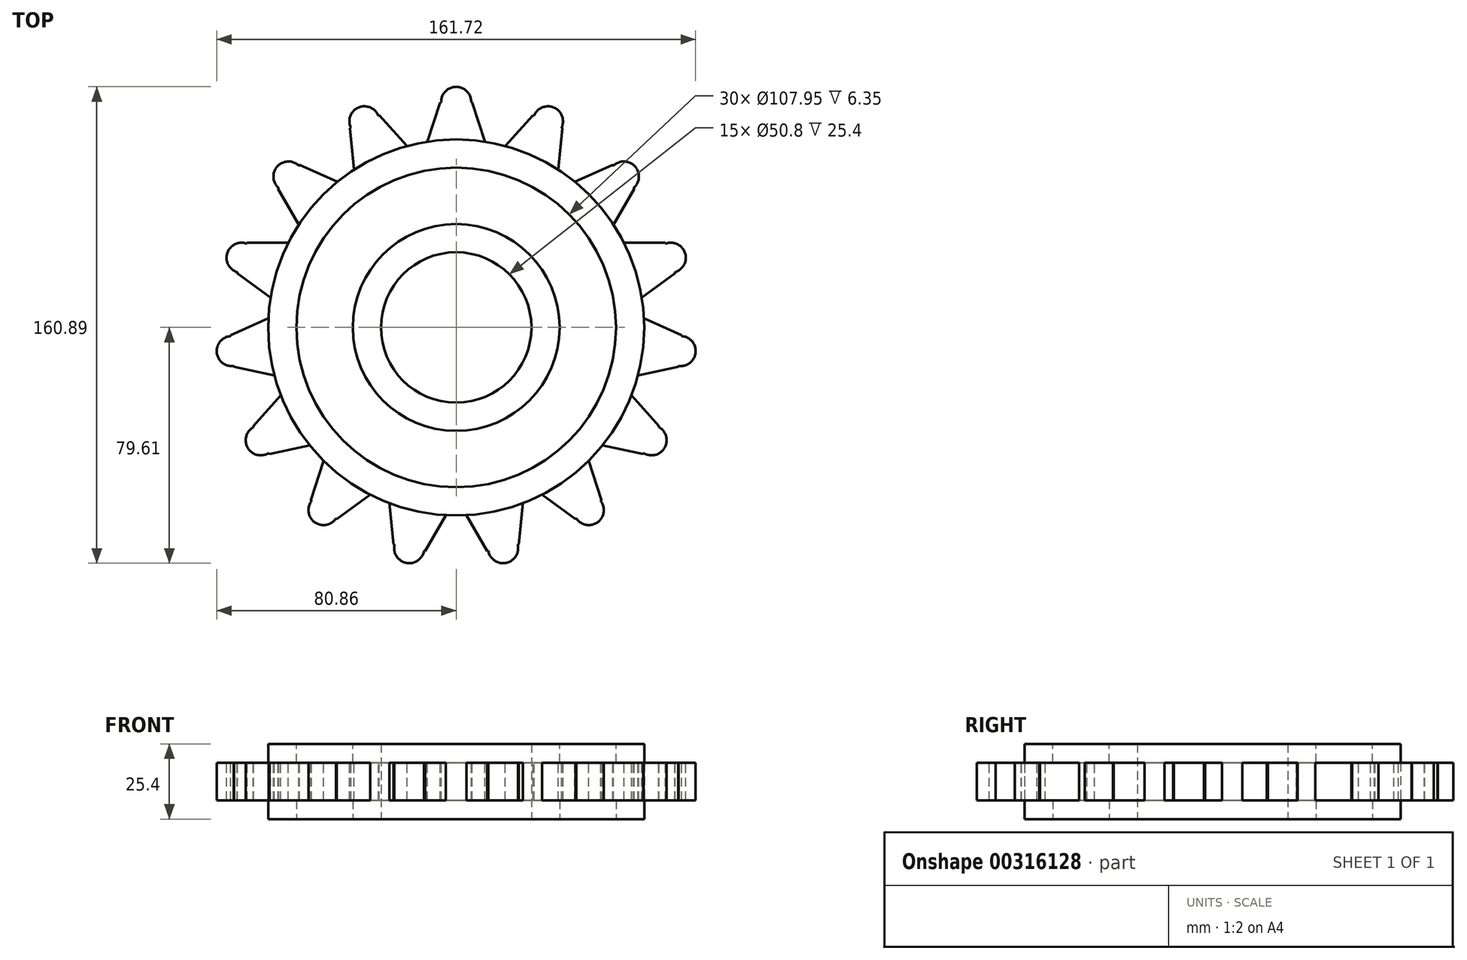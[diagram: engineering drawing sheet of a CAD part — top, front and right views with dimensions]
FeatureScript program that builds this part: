
annotation { "Feature Type Name" : "Feature", "Feature Type Description" : "" }
export const myFeature = defineFeature(function(context is Context, id is Id, definition is map)
    precondition{}
    {
        {
            var Q0;
            Q0=qCreatedBy(makeId("Top.planeOp"),FACE);
            var sketch = newSketch(context, id + "F0", { "sketchPlane" : qUnion([Q0])});
            skCircle(sketch, "E0", {"center": v(0, 0) * mm, "radius": 25.4 * mm});
            skCircle(sketch, "E1", {"center": v(0, 0) * mm, "radius": 63.5 * mm});
            skSolve(sketch);
        }
        {
            var Q0;
            Q0=makeQuery(id+"F0.imprint","IMPRINT",FACE,{"disambiguationData":[TD([[makeQuery(id+"F0.imprint","IMPRINT",EDGE,{"derivedFrom":sQuery(id+"F0.wireOp",EDGE,"E0")}),-1.0]])]});
            extrude(context, id + "F1", {"entities" : qUnion([Q0]), "depth" : 25.4 * mm});
        }
        {
            var Q0;
            Q0=makeQuery(id+"F1.opExtrude","CAP_FACE",FACE,{"disambiguationData":[OSD([sQuery(id+"F0.wireOp",EDGE,"E0"),sQuery(id+"F0.wireOp",EDGE,"E1")])],"isStart":false});
            var sketch = newSketch(context, id + "F2", { "sketchPlane" : qUnion([Q0])});
            skCircle(sketch, "E2", {"center": v(0, 0) * mm, "radius": 53.98 * mm});
            skCircle(sketch, "E3", {"center": v(0, 0) * mm, "radius": 34.93 * mm});
            skSolve(sketch);
        }
        {
            var Q0;
            Q0=makeQuery(id+"F2.imprint","IMPRINT",FACE,{"disambiguationData":[TD([[makeQuery(id+"F2.imprint","IMPRINT",EDGE,{"derivedFrom":sQuery(id+"F2.wireOp",EDGE,"E2")}),1.0]])]});
            extrude(context, id + "F3", {"entities" : qUnion([Q0]), "operationType" : NewBodyOperationType.REMOVE, "oppositeDirection" : true, "depth" : 6.35 * mm});
        }
        {
            var Q0;
            Q0=makeQuery(id+"F1.opExtrude","CAP_FACE",FACE,{"disambiguationData":[OSD([sQuery(id+"F0.wireOp",EDGE,"E0"),sQuery(id+"F0.wireOp",EDGE,"E1")])],"isStart":true});
            var sketch = newSketch(context, id + "F4", { "sketchPlane" : qUnion([Q0])});
            skCircle(sketch, "E4", {"center": v(0, 0) * mm, "radius": 34.93 * mm});
            skCircle(sketch, "E5", {"center": v(0, 0) * mm, "radius": 53.98 * mm});
            skSolve(sketch);
        }
        {
            var Q0;
            Q0 = qSketchRegion(id + "F4", true);
            var Q1;
            Q1=makeQuery(id+"F4.imprint","IMPRINT",FACE,{"disambiguationData":[TD([[makeQuery(id+"F4.imprint","IMPRINT",EDGE,{"derivedFrom":sQuery(id+"F4.wireOp",EDGE,"E4")}),-1.0]])]});
            extrude(context, id + "F5", {"entities" : qUnion([Q0, Q1]), "operationType" : NewBodyOperationType.REMOVE, "oppositeDirection" : true, "depth" : 6.35 * mm});
        }
        {
            var Q0;
            Q0=makeQuery(id+"F3.boolean.opBoolean","COPY",FACE,{"derivedFrom":makeQuery(id+"F3.opExtrude","CAP_FACE",FACE,{"disambiguationData":[OSD([sQuery(id+"F2.wireOp",EDGE,"E2"),sQuery(id+"F2.wireOp",EDGE,"E3")])],"isStart":false})});
            var sketch = newSketch(context, id + "F6", { "sketchPlane" : qUnion([Q0])});
            skArc(sketch, "E6", {"start": v(5.4, 76) * mm, "mid": v(5.24, 76.02) * mm, "end": v(5.08, 76.03) * mm});
            skArc(sketch, "E7", {"start": v(5.08, 76.03) * mm, "mid": v(0, 81.28) * mm, "end": v(-5.08, 76.03) * mm});
            skLineSegment(sketch, "E8", {"start": v(-4.83, 77.78) * mm, "end": v(-9.75, 62.75) * mm});
            skLineSegment(sketch, "E9", {"start": v(4.83, 77.78) * mm, "end": v(9.75, 62.75) * mm});
            skArc(sketch, "E10", {"start": v(9.75, 62.75) * mm, "mid": v(0, 63.5) * mm, "end": v(-9.75, 62.75) * mm});
            skArc(sketch, "E11.trimOffspring", {"start": v(-5.08, 76.03) * mm, "mid": v(-5.24, 76.02) * mm, "end": v(-5.4, 76) * mm});
            skSolve(sketch);
        }
        {
            var Q0;
            {var subQ6=sQuery(id+"F6.wireOp",EDGE,"E6");Q0=makeQuery(id+"F6.imprint","IMPRINT",FACE,{"disambiguationData":[TD([[makeQuery(id+"F6.imprint","IMPRINT",EDGE,{"derivedFrom":subQ6}),1.0]])]});}
            var sketch = newSketch(context, id + "F7", { "sketchPlane" : qUnion([Q0])});
            skSolve(sketch);
        }
        {
            var Q0;
            Q0 = qSketchRegion(id + "F7", true);
            var Q1;
            {var subQ6=sQuery(id+"F6.wireOp",EDGE,"E6");Q1=makeQuery(id+"F6.imprint","IMPRINT",FACE,{"disambiguationData":[TD([[makeQuery(id+"F6.imprint","IMPRINT",EDGE,{"derivedFrom":subQ6}),1.0]])]});}
            extrude(context, id + "F8", {"entities" : qUnion([Q0, Q1]), "operationType" : NewBodyOperationType.ADD, "oppositeDirection" : true, "depth" : 12.7 * mm});
        }
        {
            var Q0;
            Q0=makeQuery(id+"F1.opExtrude","SWEPT_BODY",BODY,{"disambiguationData":[OSD([sQuery(id+"F0.wireOp",EDGE,"E0"),sQuery(id+"F0.wireOp",EDGE,"E1")])]});
            var Q1;
            Q1=makeQuery(id+"F1.opExtrude","CAP_EDGE",EDGE,{"disambiguationData":[OSD([sQuery(id+"F0.wireOp",EDGE,"E1")])],"isStart":false});
            circularPattern(context, id + "F9", {"entities" : qUnion([Q0]), "axis" : qUnion([Q1]), "angle" : 360 * degree, "instanceCount" : 15, "equalSpace" : true});
        }
    });
